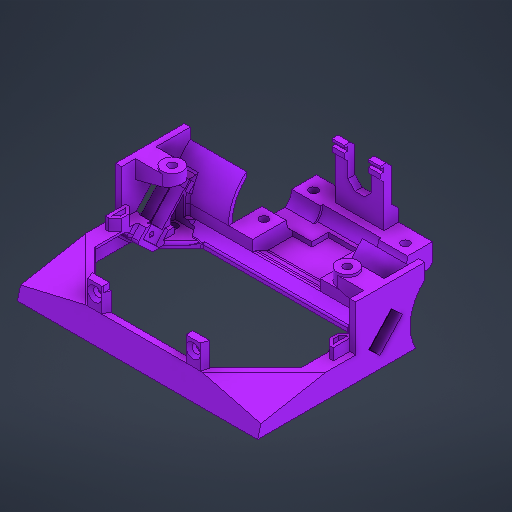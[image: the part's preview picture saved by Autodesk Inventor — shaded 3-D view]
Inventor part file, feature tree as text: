
AUTODESK INVENTOR PART (.ipt)
format: ipt  version: 2025 (Build 290162000, 162)  size: 1,860,608 bytes
history: native  units: mm
features: extrude x66, projected_geometry x60, sketch x59, other x7, chamfer x5, fillet x5, hole x2, mirror x1
ambient origin geometry x8: Origin, YZ Plane, XZ Plane, XY Plane, X Axis, Y Axis, Z Axis, Center Point
bodies: Body1 (feature_tree)
feature tree (205):
  other  "Těleso1"
  extrude  "Vysunutí1"  Depth=99.5mm
  extrude  "Vysunutí2"  Depth=67.5mm
  extrude  "Vysunutí3"  Depth=2.5mm
  extrude  "Vysunutí4"  Depth=10.0mm TaperAngle=0.0deg
  extrude  "Vysunutí5"  Depth=10.0mm TaperAngle=0.0deg
  extrude  "Vysunutí6"  Depth=5.0mm
  sketch  "Náčrt8"
  sketch  "Náčrt9"
  other  "Pracovní rovina1"
  extrude  "Vysunutí7"  TaperAngle=75.0deg  [1 undecoded]
  extrude  "Vysunutí8"  Depth=2.5mm
  extrude  "Vysunutí9"  Depth=10.0mm TaperAngle=0.0deg
  extrude  "Vysunutí10"  Depth=38.0mm
  sketch  "Náčrt15"
  extrude  "Vysunutí11"  Depth=19.0mm
  extrude  "Vysunutí12"  Depth=10.0mm TaperAngle=0.0deg
  extrude  "Vysunutí13"  Depth=1.0mm
  sketch  "Náčrt18"
  extrude  "Vysunutí14"  Depth=8.0mm
  extrude  "Vysunutí15"  Depth=10.0mm TaperAngle=0.0deg
  extrude  "Vysunutí16"  Depth=2.0mm
  extrude  "Vysunutí17"  Depth=10.0mm TaperAngle=0.0deg
  extrude  "Vysunutí19"  Depth=25.714466mm
  extrude  "Vysunutí48"  Depth=25.714466mm
  sketch  "Náčrt24"
  extrude  "Vysunutí20"  Depth=10.0mm TaperAngle=0.0deg
  extrude  "Vysunutí21"  Depth=1.5mm TaperAngle=0.0deg
  extrude  "Vysunutí29"  Depth=2.422mm
  extrude  "Vysunutí30"  Depth=1.5mm TaperAngle=0.0deg
  extrude  "Vysunutí31"  Depth=5.5mm
  sketch  "Náčrt34"
  extrude  "Vysunutí32"  Depth=7.5mm
  extrude  "Vysunutí33"  Depth=10.0mm TaperAngle=0.0deg
  extrude  "Vysunutí34"  Depth=15.5mm
  extrude  "Vysunutí74"  Depth=37.0mm
  sketch  "Náčrt36"
  sketch  "Náčrt37"
  extrude  "Vysunutí36"  Depth=1.5mm
  extrude  "Vysunutí37"  Depth=10.0mm TaperAngle=0.0deg
  extrude  "Vysunutí54"  Depth=9.0mm
  extrude  "Vysunutí39"  Depth=25.0mm TaperAngle=0.0deg
  chamfer  "Zkosení3"  Distance=6.0mm
  hole  "Díra1"  [1 undecoded]
  extrude  "Vysunutí40"  Depth=3.5mm
  extrude  "Vysunutí41"  Depth=2.5mm
  hole  "Díra3"  [1 undecoded]
  sketch  "Náčrt44"
  extrude  "Vysunutí42"  Depth=10.0mm
  extrude  "Vysunutí43"  Depth=3.5mm TaperAngle=0.0deg
  sketch  "Náčrt45"
  other  "Pracovní rovina2"
  sketch  "Náčrt46"
  extrude  "Vysunutí44"  Depth=1.0mm TaperAngle=0.0deg
  extrude  "Vysunutí45"  Depth=29.0mm
  extrude  "Vysunutí46"  Depth=9.0mm TaperAngle=0.0deg
  extrude  "Vysunutí47"  Depth=5.1mm
  sketch  "Náčrt54"
  extrude  "Vysunutí55"  Depth=16.5mm
  extrude  "Vysunutí56"  Depth=6.833mm
  extrude  "Vysunutí57"  Depth=9.0mm TaperAngle=0.0deg
  extrude  "Vysunutí58"  Depth=18.0mm
  extrude  "Vysunutí60"  Depth=10.0mm TaperAngle=0.0deg
  extrude  "Vysunutí59"  Depth=10.0mm TaperAngle=0.0deg
  sketch  "Náčrt57"
  other  "Pracovní rovina3"
  extrude  "Vysunutí62"  Depth=7.0mm TaperAngle=0.0deg
  extrude  "Vysunutí63"  Depth=14.0mm
  extrude  "Vysunutí64"  Depth=10.0mm
  extrude  "Vysunutí65"  Depth=3.5mm
  extrude  "Vysunutí66"  Depth=20.5mm
  other  "Pracovní rovina4"
  sketch  "Náčrt63"
  extrude  "Vysunutí67"  Depth=9.987mm
  extrude  "Vysunutí68"  Depth=10.0mm TaperAngle=0.0deg
  extrude  "Vysunutí84"  Depth=25.0mm
  extrude  "Vysunutí88"  Depth=2.5mm
  extrude  "Vysunutí85"  TaperAngle=45.0deg  [1 undecoded]
  extrude  "Vysunutí90"  Depth=10.0mm TaperAngle=0.0deg
  fillet  "Zaoblení6"  Radius=20.625mm
  fillet  "Zaoblení7"  Radius=5.0mm
  extrude  "Vysunutí103"  Depth=3.5mm
  sketch  "Náčrt93"
  extrude  "Vysunutí104"  TaperAngle=0.0deg  [1 undecoded]
  extrude  "Vysunutí105"  Depth=3.5mm
  extrude  "Vysunutí106"  Depth=5.0mm
  other  "Pracovní rovina5"
  extrude  "Vysunutí107"  Depth=41.0mm
  chamfer  "Zkosení8"  Distance=4.5mm
  extrude  "Vysunutí108"  Depth=4.0mm TaperAngle=0.0deg
  extrude  "Vysunutí109"  Depth=5.35mm
  other  "Pracovní rovina7"
  extrude  "Vysunutí110"  Depth=2.5mm TaperAngle=0.0deg
  mirror  "Zrcadlit1"
  extrude  "Vysunutí89"  Depth=5.5mm
  fillet  "Zaoblení8"  Radius=3.0mm
  fillet  "Zaoblení9"  [1 undecoded]
  fillet  "Zaoblení10"  Radius=2.0mm
  chamfer  "Zkosení9"  Distance=10.0mm
  chamfer  "Zkosení10"  Distance=10.0mm
  chamfer  "Zkosení11"  Distance=2.0mm Angle=45.0deg
  sketch  "Náčrt2"
  sketch  "Náčrt3"
  sketch  "Náčrt4"
  sketch  "Náčrt5"
  sketch  "Náčrt6"
  sketch  "Náčrt7"
  sketch  "Náčrt10"
  sketch  "Náčrt11"
  projected_geometry  "Promítnutá smyčka1"
  sketch  "Náčrt13"
  projected_geometry  "Promítnutá smyčka3"
  sketch  "Náčrt14"
  projected_geometry  "Promítnutá smyčka4"
  sketch  "Náčrt16"
  projected_geometry  "Promítnutá smyčka5"
  sketch  "Náčrt20"
  sketch  "Náčrt21"
  sketch  "Náčrt23"
  projected_geometry  "Promítnutá smyčka8"
  projected_geometry  "Promítnutá smyčka9"
  projected_geometry  "Promítnutá smyčka10"
  projected_geometry  "Promítnutá smyčka11"
  projected_geometry  "Promítnutá smyčka12"
  sketch  "Náčrt31"
  sketch  "Náčrt32"
  sketch  "Náčrt33"
  projected_geometry  "Promítnutá smyčka21"
  sketch  "Náčrt35"
  projected_geometry  "Promítnutá smyčka22"
  projected_geometry  "Promítnutá smyčka23"
  projected_geometry  "Promítnutá smyčka24"
  sketch  "Náčrt39"
  sketch  "Náčrt40"
  sketch  "Náčrt41"
  projected_geometry  "Promítnutá smyčka28"
  sketch  "Náčrt43"
  projected_geometry  "Promítnutá smyčka30"
  projected_geometry  "Promítnutá smyčka31"
  projected_geometry  "Promítnutá smyčka32"
  projected_geometry  "Promítnutá smyčka33"
  projected_geometry  "Promítnutá smyčka34"
  sketch  "Náčrt47"
  projected_geometry  "Promítnutá smyčka35"
  projected_geometry  "Promítnutá smyčka36"
  projected_geometry  "Promítnutá smyčka37"
  projected_geometry  "Promítnutá smyčka38"
  sketch  "Náčrt48"
  projected_geometry  "Promítnutá smyčka39"
  sketch  "Náčrt49"
  projected_geometry  "Promítnutá smyčka40"
  sketch  "Náčrt53"
  projected_geometry  "Promítnutá smyčka44"
  projected_geometry  "Promítnutá smyčka45"
  projected_geometry  "Promítnutá smyčka46"
  projected_geometry  "Promítnutá smyčka47"
  projected_geometry  "Promítnutá smyčka48"
  sketch  "Náčrt55"
  projected_geometry  "Promítnutá smyčka49"
  sketch  "Náčrt58"
  projected_geometry  "Promítnutá smyčka51"
  projected_geometry  "Promítnutá smyčka52"
  projected_geometry  "Promítnutá smyčka53"
  sketch  "Náčrt59"
  projected_geometry  "Promítnutá smyčka54"
  projected_geometry  "Promítnutá smyčka55"
  sketch  "Náčrt60"
  projected_geometry  "Promítnutá smyčka56"
  sketch  "Náčrt61"
  projected_geometry  "Promítnutá smyčka57"
  sketch  "Náčrt62"
  projected_geometry  "Promítnutá smyčka58"
  projected_geometry  "Promítnutá smyčka59"
  projected_geometry  "Promítnutá smyčka60"
  projected_geometry  "Promítnutá smyčka61"
  sketch  "Náčrt67"
  projected_geometry  "Promítnutá smyčka64"
  sketch  "Náčrt73"
  projected_geometry  "Promítnutá smyčka74"
  sketch  "Náčrt74"
  projected_geometry  "Promítnutá smyčka75"
  sketch  "Náčrt77"
  projected_geometry  "Promítnutá smyčka78"
  projected_geometry  "Promítnutá smyčka79"
  projected_geometry  "Promítnutá smyčka80"
  projected_geometry  "Promítnutá smyčka81"
  projected_geometry  "Promítnutá smyčka82"
  projected_geometry  "Promítnutá smyčka83"
  projected_geometry  "Promítnutá smyčka84"
  sketch  "Náčrt78"
  projected_geometry  "Promítnutá smyčka85"
  sketch  "Náčrt79"
  projected_geometry  "Promítnutá smyčka86"
  sketch  "Náčrt92"
  projected_geometry  "Promítnutá smyčka116"
  projected_geometry  "Promítnutá smyčka117"
  projected_geometry  "Promítnutá smyčka118"
  sketch  "Náčrt94"
  projected_geometry  "Promítnutá smyčka119"
  projected_geometry  "Promítnutá smyčka120"
  sketch  "Náčrt95"
  sketch  "Náčrt96"
  sketch  "Náčrt97"
  projected_geometry  "Promítnutá smyčka121"
  sketch  "Náčrt98"
note: 6 required parameter values undecoded (feature->parameter linkage not recoverable at this tier; creation-order binding heuristic only, values carry confidence <= 0.55)
